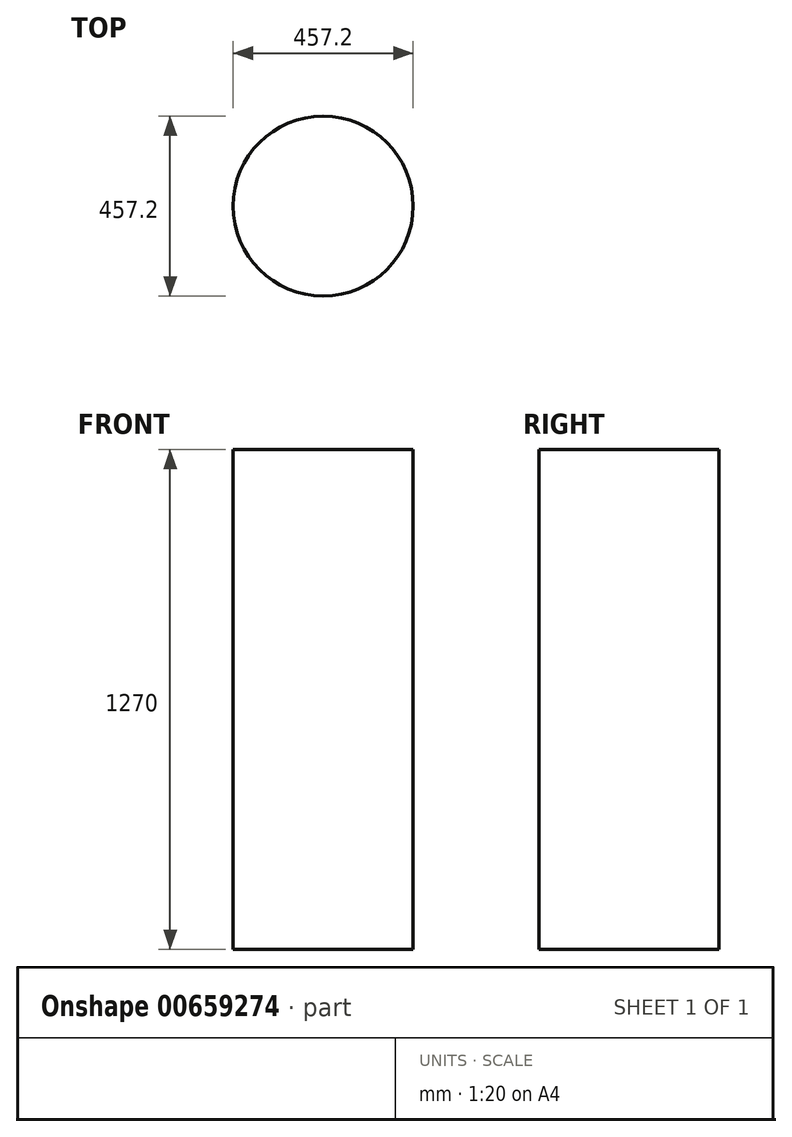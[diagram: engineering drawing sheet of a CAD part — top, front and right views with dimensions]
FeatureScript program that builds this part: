
annotation { "Feature Type Name" : "Feature", "Feature Type Description" : "" }
export const myFeature = defineFeature(function(context is Context, id is Id, definition is map)
    precondition{}
    {
        {
            var Q0;
            Q0=qCreatedBy(makeId("Front.planeOp"),FACE);
            var sketch = newSketch(context, id + "F0", { "sketchPlane" : qUnion([Q0])});
            skLineSegment(sketch, "E0.bottom", {"start": v(0, 635) * mm, "end": v(228.6, 635) * mm});
            skLineSegment(sketch, "E0.top", {"start": v(0, -635) * mm, "end": v(228.6, -635) * mm});
            skLineSegment(sketch, "E0.left", {"start": v(0, 635) * mm, "end": v(0, -635) * mm});
            skLineSegment(sketch, "E0.right", {"start": v(228.6, 635) * mm, "end": v(228.6, -635) * mm});
            skSolve(sketch);
        }
        {
            var Q0;
            Q0=makeQuery(id+"F0.imprint","IMPRINT",FACE,{"disambiguationData":[TD([[makeQuery(id+"F0.imprint","IMPRINT",EDGE,{"derivedFrom":sQuery(id+"F0.wireOp",EDGE,"E0.bottom")}),-1.0]])]});
            var Q1;
            Q1=sQuery(id+"F0.wireOp",EDGE,"E0.left");
            revolve(context, id + "F1", {"entities" : qUnion([Q0]), "axis" : qUnion([Q1]), "revolveType" : RevolveType.FULL});
        }
    });
